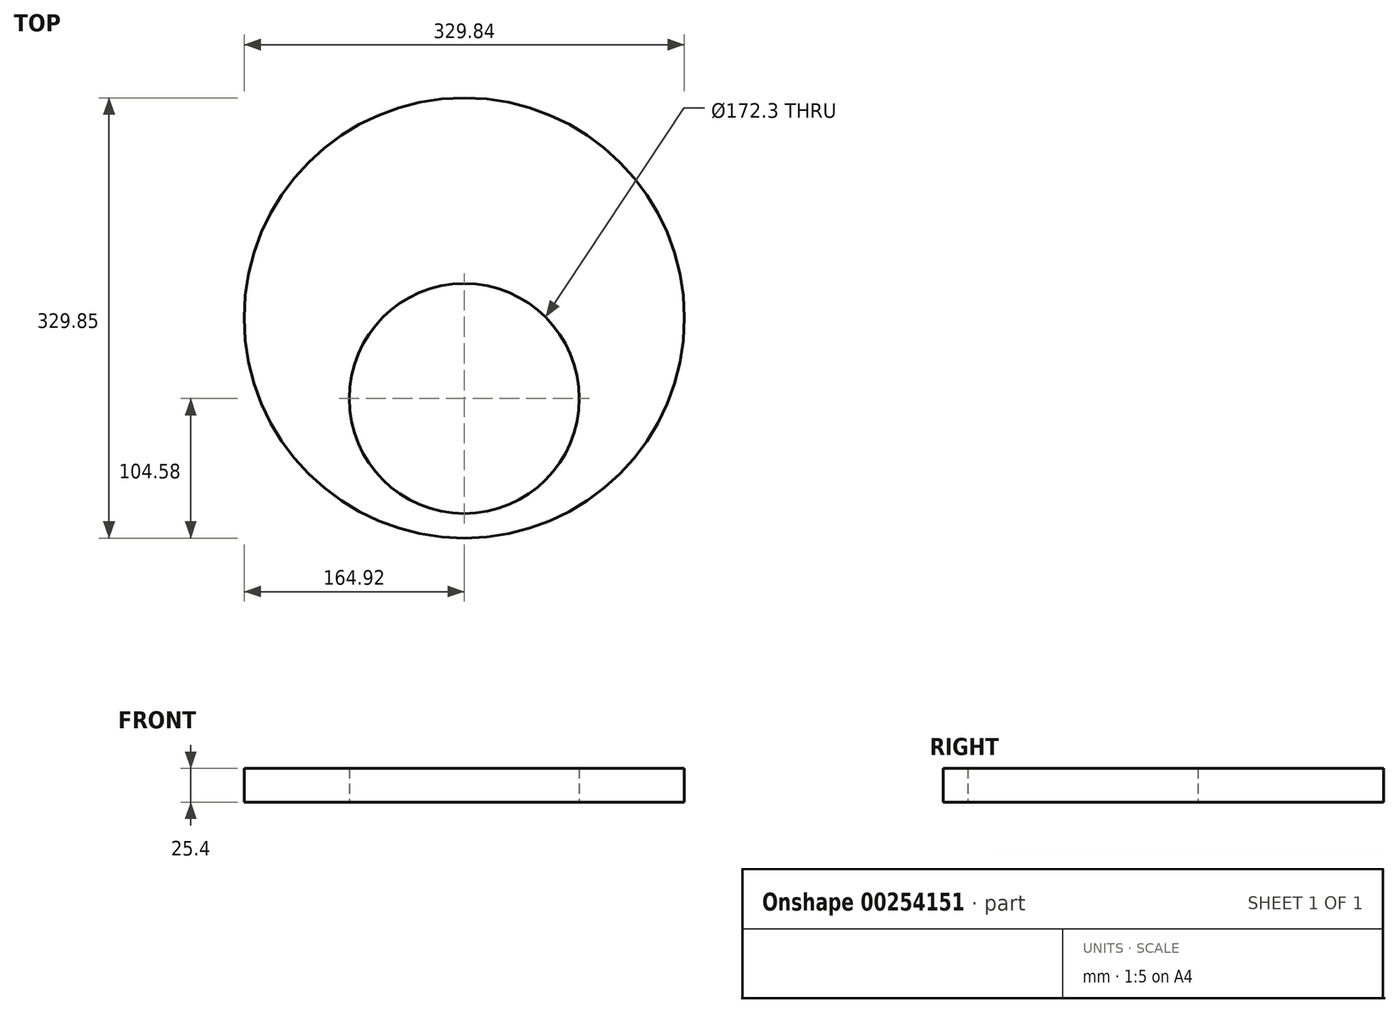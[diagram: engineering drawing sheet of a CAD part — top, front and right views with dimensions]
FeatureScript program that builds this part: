
annotation { "Feature Type Name" : "Feature", "Feature Type Description" : "" }
export const myFeature = defineFeature(function(context is Context, id is Id, definition is map)
    precondition{}
    {
        {
            var Q0;
            Q0=qCreatedBy(makeId("Top.planeOp"),FACE);
            var sketch = newSketch(context, id + "F0", { "sketchPlane" : qUnion([Q0])});
            skCircle(sketch, "E0", {"center": v(0, 0) * mm, "radius": 86.15 * mm});
            skCircle(sketch, "E1", {"center": v(0, 60.35) * mm, "radius": 164.92 * mm});
            skSolve(sketch);
        }
        {
            var Q0;
            Q0 = qSketchRegion(id + "F0", true);
            extrude(context, id + "F1", {"entities" : qUnion([Q0]), "depth" : 25.4 * mm});
        }
    });
